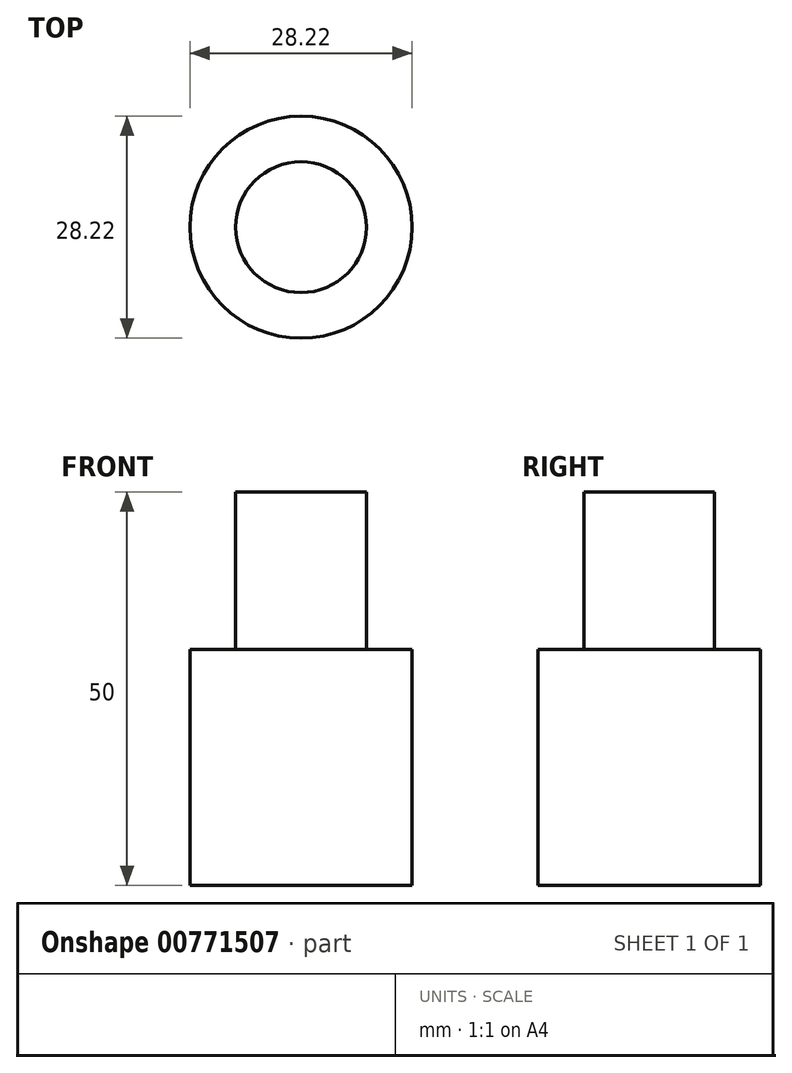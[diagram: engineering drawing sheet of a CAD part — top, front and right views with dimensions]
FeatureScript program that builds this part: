
annotation { "Feature Type Name" : "Feature", "Feature Type Description" : "" }
export const myFeature = defineFeature(function(context is Context, id is Id, definition is map)
    precondition{}
    {
        {
            var Q0;
            Q0=qCreatedBy(makeId("Top.planeOp"),FACE);
            var sketch = newSketch(context, id + "F0", { "sketchPlane" : qUnion([Q0])});
            skCircle(sketch, "E0", {"center": v(0, 0) * mm, "radius": 14.1 * mm});
            skSolve(sketch);
        }
        {
            var Q0;
            Q0=makeQuery(id+"F0.imprint","IMPRINT",FACE,{"disambiguationData":[TD([[makeQuery(id+"F0.imprint","IMPRINT",EDGE,{"derivedFrom":sQuery(id+"F0.wireOp",EDGE,"E0")}),1.0]])]});
            extrude(context, id + "F1", {"entities" : qUnion([Q0]), "endBound" : BoundingType.SYMMETRIC, "depth" : 30 * mm, "offsetDistance" : 25.4 * mm});
        }
        {
            var Q0;
            Q0=makeQuery(id+"F1.opExtrude","CAP_FACE",FACE,{"disambiguationData":[OSD([sQuery(id+"F0.wireOp",EDGE,"E0")])],"isStart":false});
            var sketch = newSketch(context, id + "F2", { "sketchPlane" : qUnion([Q0])});
            skCircle(sketch, "E1", {"center": v(0, 0) * mm, "radius": 8.31 * mm});
            skSolve(sketch);
        }
        {
            var Q0;
            Q0=makeQuery(id+"F2.imprint","IMPRINT",FACE,{"disambiguationData":[TD([[makeQuery(id+"F2.imprint","IMPRINT",EDGE,{"derivedFrom":sQuery(id+"F2.wireOp",EDGE,"E1")}),1.0]])]});
            extrude(context, id + "F3", {"entities" : qUnion([Q0]), "operationType" : NewBodyOperationType.ADD, "endBound" : BoundingType.SYMMETRIC, "depth" : 40 * mm, "offsetDistance" : 25.4 * mm});
        }
    });
